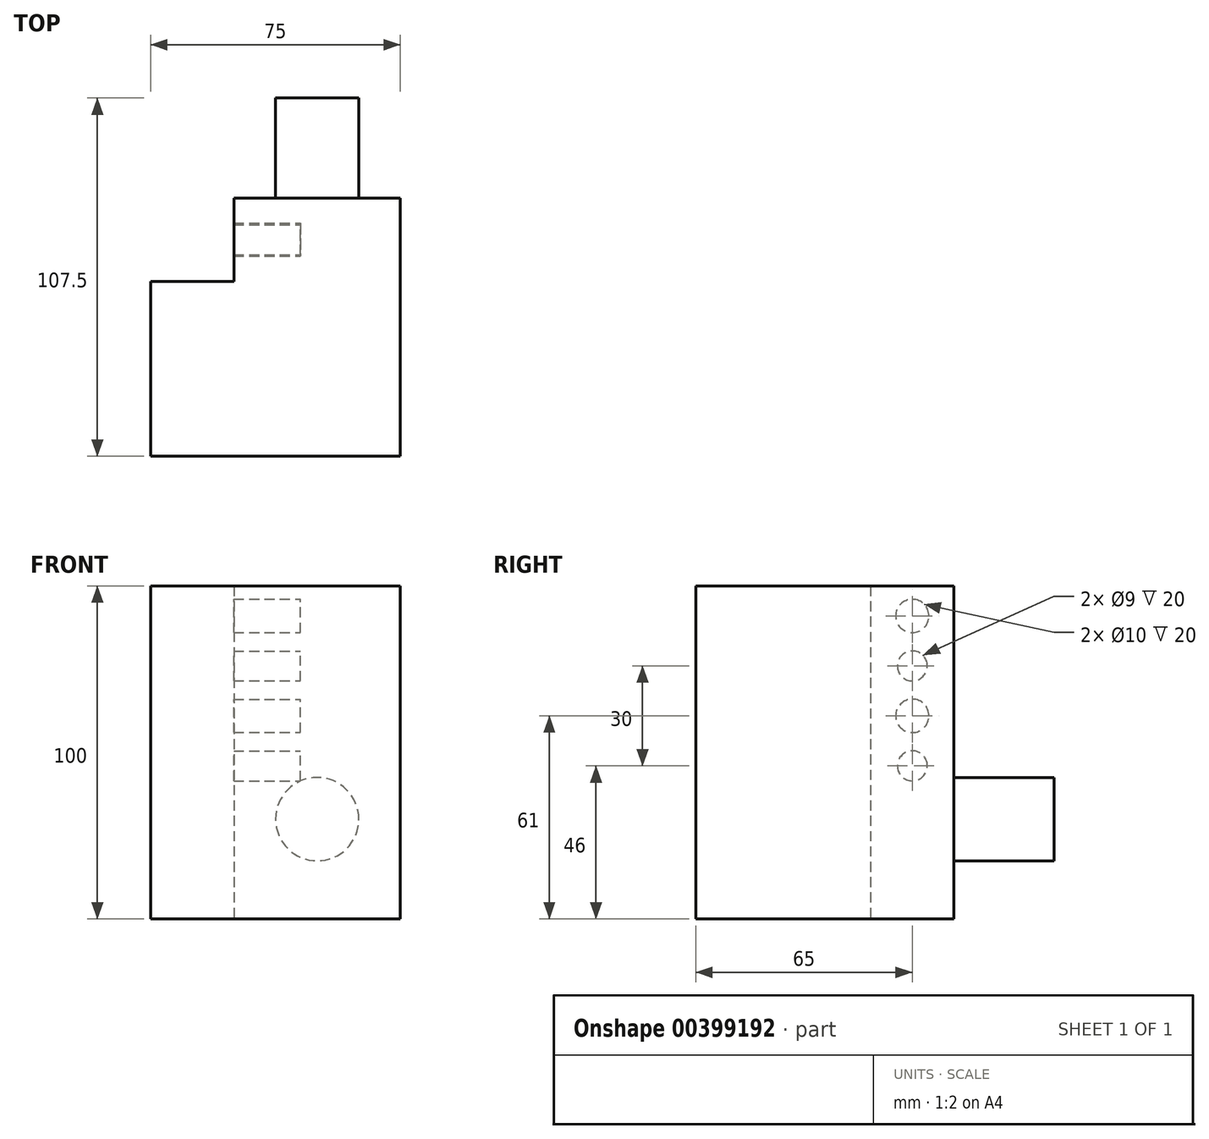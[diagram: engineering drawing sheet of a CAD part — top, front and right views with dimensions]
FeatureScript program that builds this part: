
annotation { "Feature Type Name" : "Feature", "Feature Type Description" : "" }
export const myFeature = defineFeature(function(context is Context, id is Id, definition is map)
    precondition{}
    {
        {
            var Q0;
            Q0=qCreatedBy(makeId("Top.planeOp"),FACE);
            var sketch = newSketch(context, id + "F0", { "sketchPlane" : qUnion([Q0])});
            skLineSegment(sketch, "E0.bottom", {"start": v(0, 0) * mm, "end": v(20, 0) * mm});
            skLineSegment(sketch, "E0.top", {"start": v(0, -25) * mm, "end": v(20, -25) * mm});
            skLineSegment(sketch, "E0.left", {"start": v(0, 0) * mm, "end": v(0, -25) * mm});
            skLineSegment(sketch, "E0.right", {"start": v(20, 0) * mm, "end": v(20, -25) * mm});
            skSolve(sketch);
        }
        {
            var Q0;
            Q0=qSketchRegion(id+"F0",true);
            extrude(context, id + "F1", {"entities" : qUnion([Q0]), "depth" : 80 * mm});
        }
        {
            var Q0;
            Q0=makeQuery(id+"F1.opExtrude","SWEPT_FACE",FACE,{"disambiguationData":[OSD([sQuery(id+"F0.wireOp",EDGE,"E0.right")])]});
            var sketch = newSketch(context, id + "F2", { "sketchPlane" : qUnion([Q0])});
            skLineSegment(sketch, "E1", {"start": v(-12.5, 80) * mm, "end": v(-12.5, 71) * mm, "construction": true});
            skPoint(sketch, "E1.endSnap0", {"position": v(-12.5, 80) * mm});
            skLineSegment(sketch, "E2", {"start": v(-12.5, 71) * mm, "end": v(-12.5, 56) * mm, "construction": true});
            skLineSegment(sketch, "E3", {"start": v(-12.5, 56) * mm, "end": v(-12.5, 41) * mm, "construction": true});
            skLineSegment(sketch, "E4", {"start": v(-12.5, 41) * mm, "end": v(-12.5, 26) * mm, "construction": true});
            skLineSegment(sketch, "E5", {"start": v(-12.5, 26) * mm, "end": v(-12.5, 0) * mm, "construction": true});
            skCircle(sketch, "E6", {"center": v(-12.5, 71) * mm, "radius": 5 * mm});
            skCircle(sketch, "E7", {"center": v(-12.5, 56) * mm, "radius": 4.5 * mm});
            skCircle(sketch, "E8", {"center": v(-12.5, 41) * mm, "radius": 5 * mm});
            skCircle(sketch, "E9", {"center": v(-12.5, 26) * mm, "radius": 4.5 * mm});
            skSolve(sketch);
        }
        {
            var Q0;
            Q0=qSketchRegion(id+"F2",true);
            extrude(context, id + "F3", {"entities" : qUnion([Q0]), "operationType" : NewBodyOperationType.REMOVE, "oppositeDirection" : true, "depth" : 25 * mm});
        }
        {
            var Q0;
            Q0=makeQuery(id+"F1.opExtrude","SWEPT_FACE",FACE,{"disambiguationData":[OSD([sQuery(id+"F0.wireOp",EDGE,"E0.top")])]});
            var sketch = newSketch(context, id + "F4", { "sketchPlane" : qUnion([Q0])});
            skLineSegment(sketch, "E10", {"start": v(0, 0) * mm, "end": v(-25, 0) * mm});
            skLineSegment(sketch, "E11", {"start": v(-25, 0) * mm, "end": v(-25, 80) * mm});
            skLineSegment(sketch, "E12", {"start": v(-25, 80) * mm, "end": v(50, 80) * mm});
            skLineSegment(sketch, "E13", {"start": v(50, 80) * mm, "end": v(50, 0) * mm});
            skLineSegment(sketch, "E14", {"start": v(50, 0) * mm, "end": v(0, 0) * mm});
            skSolve(sketch);
        }
        {
            var Q0;
            Q0 = qSketchRegion(id + "F4", true);
            extrude(context, id + "F5", {"entities" : qUnion([Q0]), "operationType" : NewBodyOperationType.ADD, "depth" : 52.5 * mm});
        }
        {
            var Q0;
            Q0=makeQuery(id+"F1.opExtrude","SWEPT_FACE",FACE,{"disambiguationData":[OSD([sQuery(id+"F0.wireOp",EDGE,"E0.right")])]});
            var sketch = newSketch(context, id + "F6", { "sketchPlane" : qUnion([Q0])});
            skLineSegment(sketch, "E15.bottom", {"start": v(0, 80) * mm, "end": v(-25, 80) * mm});
            skLineSegment(sketch, "E15.top", {"start": v(0, 0) * mm, "end": v(-25, 0) * mm});
            skLineSegment(sketch, "E15.left", {"start": v(0, 80) * mm, "end": v(0, 0) * mm});
            skLineSegment(sketch, "E15.right", {"start": v(-25, 80) * mm, "end": v(-25, 0) * mm});
            skSolve(sketch);
        }
        {
            var Q0;
            Q0 = qSketchRegion(id + "F6", true);
            extrude(context, id + "F7", {"entities" : qUnion([Q0]), "operationType" : NewBodyOperationType.ADD, "depth" : 30 * mm});
        }
        {
            var Q0;
            Q0=makeQuery(id+"F7.boolean.opBoolean","MERGE",FACE,{"derivedFrom":[makeQuery(id+"F5.boolean.opBoolean","MERGE",FACE,{"derivedFrom":[makeQuery(id+"F1.opExtrude","CAP_FACE",FACE,{"disambiguationData":[OSD([sQuery(id+"F0.wireOp",EDGE,"E0.bottom"),sQuery(id+"F0.wireOp",EDGE,"E0.top"),sQuery(id+"F0.wireOp",EDGE,"E0.left"),sQuery(id+"F0.wireOp",EDGE,"E0.right")])],"isStart":true}),makeQuery(id+"F5.opExtrude","SWEPT_FACE",FACE,{"disambiguationData":[OSD([sQuery(id+"F4.wireOp",EDGE,"E10"),sQuery(id+"F4.wireOp",EDGE,"E14")])]})]}),makeQuery(id+"F7.opExtrude","SWEPT_FACE",FACE,{"disambiguationData":[OSD([sQuery(id+"F6.wireOp",EDGE,"E15.top")])]})]});
            var sketch = newSketch(context, id + "F8", { "sketchPlane" : qUnion([Q0])});
            skLineSegment(sketch, "E16", {"start": v(-25, 25) * mm, "end": v(-25, 77.5) * mm});
            skLineSegment(sketch, "E17", {"start": v(-25, 77.5) * mm, "end": v(50, 77.5) * mm});
            skLineSegment(sketch, "E18", {"start": v(50, 77.5) * mm, "end": v(50, 0) * mm});
            skLineSegment(sketch, "E19", {"start": v(50, 0) * mm, "end": v(0, 0) * mm});
            skLineSegment(sketch, "E20", {"start": v(0, 0) * mm, "end": v(0, 25) * mm});
            skLineSegment(sketch, "E21", {"start": v(0, 25) * mm, "end": v(-25, 25) * mm});
            skSolve(sketch);
        }
        {
            var Q0;
            Q0 = qSketchRegion(id + "F8", true);
            extrude(context, id + "F9", {"entities" : qUnion([Q0]), "operationType" : NewBodyOperationType.ADD, "depth" : 20 * mm});
        }
        {
            var Q0;
            Q0=makeQuery(id+"F9.boolean.opBoolean","MERGE",FACE,{"derivedFrom":[makeQuery(id+"F7.boolean.opBoolean","MERGE",FACE,{"derivedFrom":[makeQuery(id+"F1.opExtrude","SWEPT_FACE",FACE,{"disambiguationData":[OSD([sQuery(id+"F0.wireOp",EDGE,"E0.bottom")])]}),makeQuery(id+"F7.opExtrude","SWEPT_FACE",FACE,{"disambiguationData":[OSD([sQuery(id+"F6.wireOp",EDGE,"E15.left")])]})]}),makeQuery(id+"F9.opExtrude","SWEPT_FACE",FACE,{"disambiguationData":[OSD([sQuery(id+"F8.wireOp",EDGE,"E19")])]})]});
            var sketch = newSketch(context, id + "F10", { "sketchPlane" : qUnion([Q0])});
            skLineSegment(sketch, "E22", {"start": v(-25, -20) * mm, "end": v(-25, 10) * mm, "construction": true});
            skCircle(sketch, "E23", {"center": v(-25, 10) * mm, "radius": 12.5 * mm});
            skSolve(sketch);
        }
        {
            var Q0;
            Q0=makeQuery(id+"F10.imprint","IMPRINT",FACE,{"disambiguationData":[TD([[makeQuery(id+"F10.imprint","IMPRINT",EDGE,{"derivedFrom":sQuery(id+"F10.wireOp",EDGE,"E23")}),1.0]])]});
            extrude(context, id + "F11", {"entities" : qUnion([Q0]), "operationType" : NewBodyOperationType.ADD, "depth" : 30 * mm});
        }
    });
